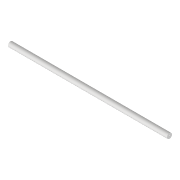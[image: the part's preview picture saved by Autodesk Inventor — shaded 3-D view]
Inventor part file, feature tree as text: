
AUTODESK INVENTOR PART (.ipt)
format: ipt  version: 2022 (Build 260153000, 153)  size: 77,312 bytes
history: native  units: mm
features: extrude x1, plane x1, sketch x1
ambient origin geometry x8: Origin, YZ Plane, XZ Plane, XY Plane, X Axis, Y Axis, Z Axis, Center Point
bodies: Solid1 (feature_tree)
feature tree (3):
  extrude  "Extrusion1"  Depth=70.0mm
  plane  "Work Plane1"
  sketch  "Sketch1"  dims[d0=2.2mm d1=0.5mm d2=70.0mm d3=0.0mm]
